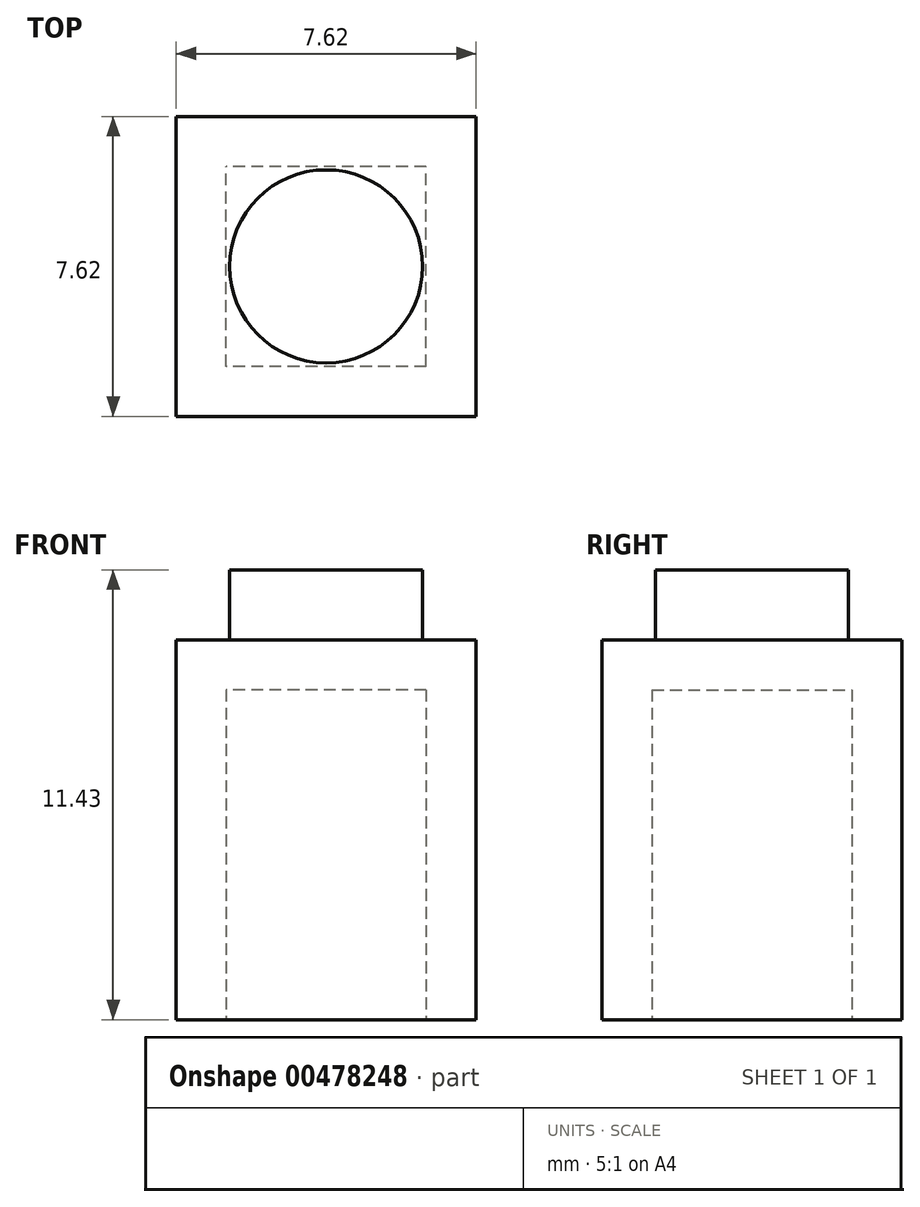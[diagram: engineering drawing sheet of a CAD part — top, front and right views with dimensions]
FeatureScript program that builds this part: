
annotation { "Feature Type Name" : "Feature", "Feature Type Description" : "" }
export const myFeature = defineFeature(function(context is Context, id is Id, definition is map)
    precondition{}
    {
        {
            var Q0;
            Q0=qCreatedBy(makeId("Top.planeOp"),FACE);
            var sketch = newSketch(context, id + "F0", { "sketchPlane" : qUnion([Q0])});
            skLineSegment(sketch, "E0.bottom", {"start": v(3.81, -3.8) * mm, "end": v(-3.81, -3.8) * mm});
            skLineSegment(sketch, "E0.top", {"start": v(3.81, 3.8) * mm, "end": v(-3.81, 3.8) * mm});
            skLineSegment(sketch, "E0.left", {"start": v(3.81, -3.8) * mm, "end": v(3.81, 3.8) * mm});
            skLineSegment(sketch, "E0.right", {"start": v(-3.81, -3.8) * mm, "end": v(-3.81, 3.8) * mm});
            skPoint(sketch, "E0.middle", {"position": v(0, 0) * mm});
            skSolve(sketch);
        }
        {
            var Q0;
            Q0 = qSketchRegion(id + "F0", true);
            extrude(context, id + "F1", {"entities" : qUnion([Q0]), "depth" : 9.65 * mm});
        }
        {
            var Q0;
            Q0=makeQuery(id+"F1.opExtrude","CAP_FACE",FACE,{"disambiguationData":[OSD([sQuery(id+"F0.wireOp",EDGE,"E0.bottom"),sQuery(id+"F0.wireOp",EDGE,"E0.top"),sQuery(id+"F0.wireOp",EDGE,"E0.left"),sQuery(id+"F0.wireOp",EDGE,"E0.right")])],"isStart":false});
            var sketch = newSketch(context, id + "F2", { "sketchPlane" : qUnion([Q0])});
            skCircle(sketch, "E1", {"center": v(0, 0) * mm, "radius": 2.45 * mm});
            skSolve(sketch);
        }
        {
            var Q0;
            Q0 = qSketchRegion(id + "F2", true);
            extrude(context, id + "F3", {"entities" : qUnion([Q0]), "operationType" : NewBodyOperationType.ADD, "depth" : 1.78 * mm});
        }
        {
            var Q0;
            Q0=makeQuery(id+"F1.opExtrude","CAP_FACE",FACE,{"disambiguationData":[OSD([sQuery(id+"F0.wireOp",EDGE,"E0.bottom"),sQuery(id+"F0.wireOp",EDGE,"E0.top"),sQuery(id+"F0.wireOp",EDGE,"E0.left"),sQuery(id+"F0.wireOp",EDGE,"E0.right")])],"isStart":true});
            var sketch = newSketch(context, id + "F4", { "sketchPlane" : qUnion([Q0])});
            skLineSegment(sketch, "E2.bottom", {"start": v(2.54, 2.54) * mm, "end": v(-2.54, 2.54) * mm});
            skLineSegment(sketch, "E2.top", {"start": v(2.54, -2.54) * mm, "end": v(-2.54, -2.54) * mm});
            skLineSegment(sketch, "E2.left", {"start": v(2.54, 2.54) * mm, "end": v(2.54, -2.54) * mm});
            skLineSegment(sketch, "E2.right", {"start": v(-2.54, 2.54) * mm, "end": v(-2.54, -2.54) * mm});
            skPoint(sketch, "E2.middle", {"position": v(0, 0) * mm});
            skSolve(sketch);
        }
        {
            var Q0;
            Q0 = qSketchRegion(id + "F4", true);
            extrude(context, id + "F5", {"entities" : qUnion([Q0]), "operationType" : NewBodyOperationType.REMOVE, "oppositeDirection" : true, "depth" : 8.38 * mm, "offsetDistance" : 25.4 * mm});
        }
    });
